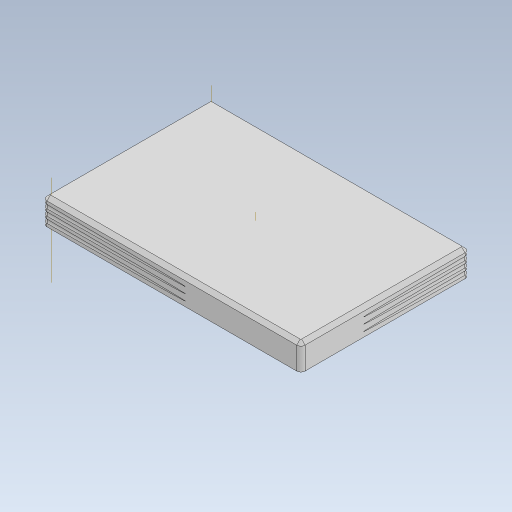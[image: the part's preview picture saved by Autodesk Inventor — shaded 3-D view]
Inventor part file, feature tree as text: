
AUTODESK INVENTOR PART (.ipt)
format: ipt  version: 2023 (Build 270158030, 158C)  size: 513,536 bytes
history: native  units: mm
features: projected_geometry x28, sketch x12, extrude x11, chamfer x5, other x4, plane x2, revolve x2, pattern_circular x2, fillet x1
ambient origin geometry x8: Origin, YZ Plane, XZ Plane, XY Plane, X Axis, Y Axis, Z Axis, Center Point
bodies: Solid1 (feature_tree)
feature tree (67):
  extrude  "Extrusion1"  Depth=112.0mm
  extrude  "Extrusion2"  Depth=88.0mm
  extrude  "Extrusion3"  Depth=45.0mm
  fillet  "Fillet1"  Radius=2.0mm
  extrude  "Extrusion4"  Depth=3.0mm
  extrude  "Extrusion5"  Depth=1.5mm TaperAngle=45.0deg
  chamfer  "Chamfer1"  Distance=15.0mm
  chamfer  "Chamfer2"  Distance=1.5mm Angle=45.0deg
  chamfer  "Chamfer3"  Distance=1.0mm Angle=45.0deg
  extrude  "Extrusion6"  Depth=16.5mm TaperAngle=0.0deg
  extrude  "Extrusion7"  Depth=2.5mm TaperAngle=45.0deg
  chamfer  "Chamfer4"  Distance=4.5mm
  chamfer  "Chamfer5"  Distance=5.0mm
  other  "Work Axis1"
  plane  "Work Plane1"
  revolve  "Revolution1"  [1 undecoded]
  extrude  "Extrusion8"  TaperAngle=90.0deg  [1 undecoded]
  extrude  "Extrusion9"  Depth=3.0mm
  pattern_circular  "Circular Pattern1"  [2 undecoded]
  other  "Work Axis2"
  plane  "Work Plane2"
  revolve  "Revolution2"  Angle=360.0deg
  extrude  "Extrusion10"  Depth=3.0mm
  extrude  "Extrusion11"  Depth=3.0mm
  pattern_circular  "Circular Pattern2"  [2 undecoded]
  sketch  "Sketch1"  dims[d0=176.0mm d1=112.0mm]
  sketch  "Sketch2"  dims[d2=56.0mm d3=88.0mm]
  projected_geometry  "Projected Loop1"
  sketch  "Sketch3"  dims[d4=45.0mm d5=0.0mm d6=4.0mm d7=2.0mm d8=0.0mm]
  other  "box"
  sketch  "Sketch4"  dims[d10=45.0mm d11=0.0mm d12=3.0mm]
  projected_geometry  "Projected Loop5"
  projected_geometry  "Projected Loop6"
  projected_geometry  "Projected Loop7"
  sketch  "Sketch6"  dims[d14=15.0mm d15=0.0mm d16=1.5mm d17=2.0mm d18=45.0deg d19=15.0mm d20=0.0mm]
  projected_geometry  "Projected Loop8"
  projected_geometry  "Projected Loop9"
  projected_geometry  "Projected Loop10"
  projected_geometry  "Projected Loop11"
  projected_geometry  "Projected Loop12"
  projected_geometry  "Projected Loop13"
  projected_geometry  "Projected Loop14"
  projected_geometry  "Projected Loop15"
  other  "lid"
  sketch  "Sketch7"  dims[d21=1.0mm]
  projected_geometry  "Projected Loop16"
  sketch  "Sketch8"  dims[d24=1.5mm]
  sketch  "Sketch9"  dims[d25=1.5mm d26=1.5mm d27=2.0mm d28=45.0deg d29=1.0mm d30=2.0mm d31=45.0deg]
  projected_geometry  "Projected Loop17"
  projected_geometry  "Projected Loop18"
  projected_geometry  "Projected Loop19"
  sketch  "Sketch10"  dims[d32=2.0mm d33=0.0mm d34=16.5mm d35=0.0mm]
  projected_geometry  "Projected Loop20"
  projected_geometry  "Projected Loop21"
  projected_geometry  "Projected Loop22"
  sketch  "Sketch11"  dims[d36=1.5mm d37=2.0mm d38=45.0deg d39=2.5mm d40=2.0mm d41=45.0deg]
  sketch  "Sketch12"  dims[d42=3.5mm]
  projected_geometry  "Projected Loop23"
  projected_geometry  "Projected Loop24"
  projected_geometry  "Projected Loop25"
  projected_geometry  "Projected Loop26"
  projected_geometry  "Projected Loop27"
  sketch  "Sketch13"  dims[d43=4.5mm d44=4.5mm d45=5.0mm d46=3.0mm d47=90.0deg d48=3.0mm d49=-0.038397mm d50=0.0mm d51=-0.05236mm d52=20.0mm d53=360.0deg d55=1.5mm d56=2.7mm d57=2.7mm d58=2.7mm d59=2.7mm d60=2.0mm d61=90.0deg d62=4.304mm d63=-0.034907mm d64=19.689mm d65=-0.05236mm d66=20.0mm d67=360.0deg]
  projected_geometry  "Projected Loop28"
  projected_geometry  "Projected Loop29"
  projected_geometry  "Projected Loop30"
  projected_geometry  "Projected Loop31"
note: 6 required parameter values undecoded (feature->parameter linkage not recoverable at this tier; creation-order binding heuristic only, values carry confidence <= 0.55)